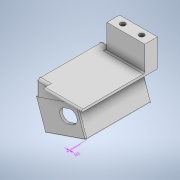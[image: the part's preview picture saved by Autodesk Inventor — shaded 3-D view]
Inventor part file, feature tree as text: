
AUTODESK INVENTOR PART (.ipt)
format: ipt  version: 2020 (Build 240168000, 168)  size: 239,616 bytes
history: native  units: in
note: dims shown in document units (in); Inventor stores cm internally (conversion verified against a paired STEP export)
features: other x5, fillet x5, extrude x1, sketch x1
ambient origin geometry x8: Origin, YZ Plane, XZ Plane, XY Plane, X Axis, Y Axis, Z Axis, Center Point
bodies: Solid1 (feature_tree), Solid2 (feature_tree)
feature tree (12):
  other  "GoPro.iam"
  other  "GoProCase.ipt:1"
  other  "Base.ipt:1"
  other  "Annotations"
  fillet  "Fillet1"  Radius=0.3937in
  extrude  "Extrusion1"  Depth=0.15in
  fillet  "Fillet2"  Radius=1.0in
  fillet  "Fillet3"  Radius=0.1in
  fillet  "Fillet4"  Radius=0.1in
  fillet  "Fillet5"  Radius=0.04in
  sketch  "Sketch1"  dims[d1=0.05in d2=0.1in d3=1.0in d4=0.0in d5=0.1in d6=0.1in d9=0.04in d10=0.15in d7=0.1708in d8=0.0308in]
  other  "Linear Dimension 1"
